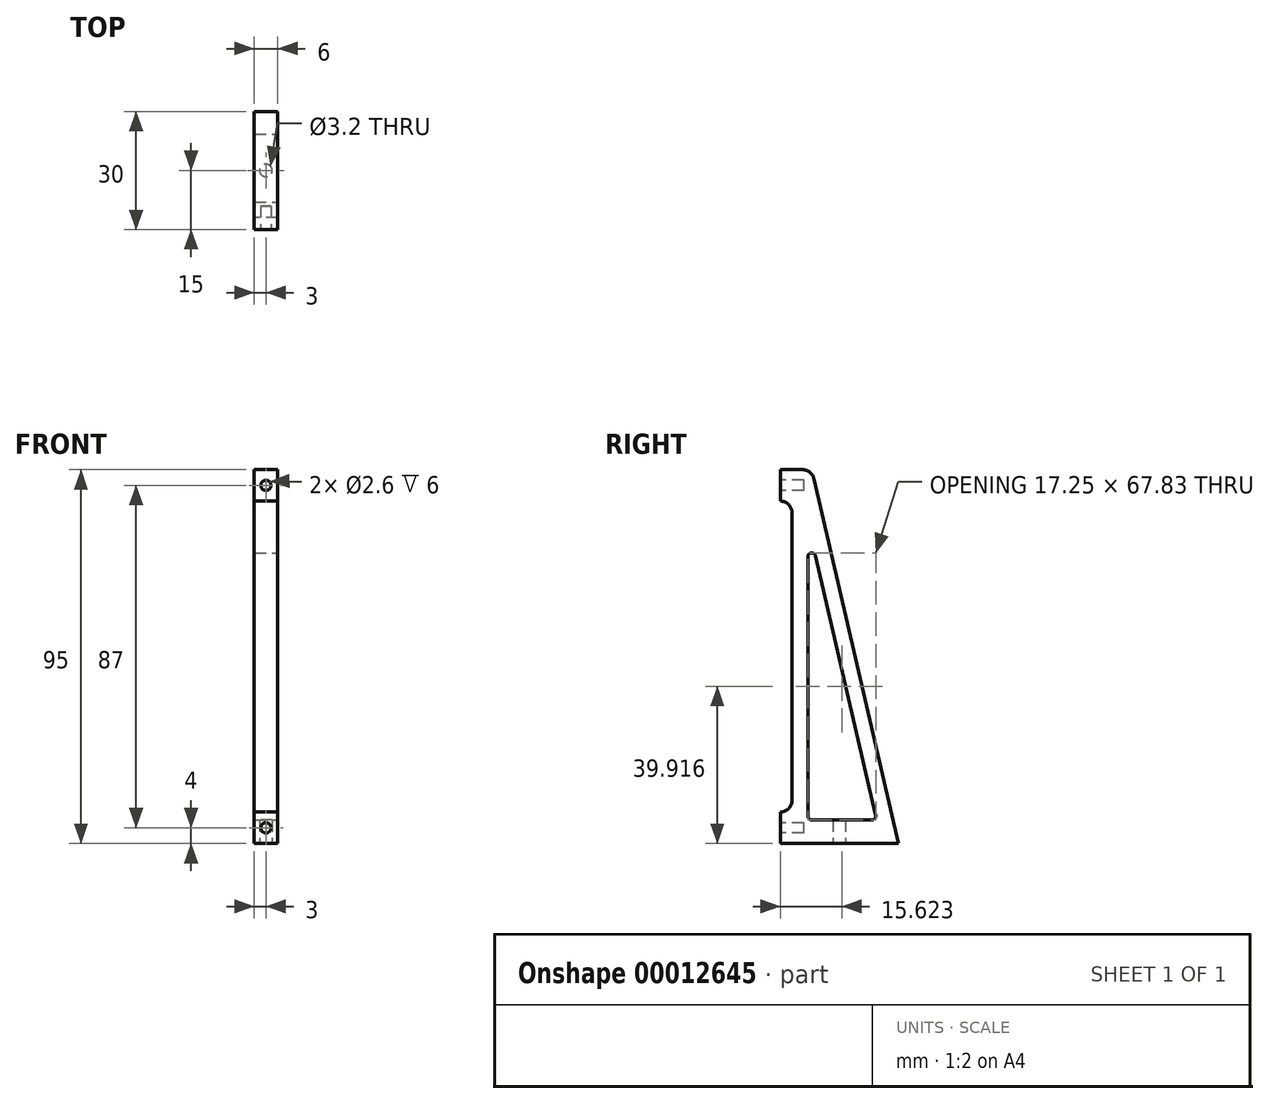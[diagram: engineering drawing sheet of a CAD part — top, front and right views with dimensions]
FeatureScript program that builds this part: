
annotation { "Feature Type Name" : "Feature", "Feature Type Description" : "" }
export const myFeature = defineFeature(function(context is Context, id is Id, definition is map)
    precondition{}
    {
        {
            var Q0;
            Q0=qCreatedBy(makeId("Right.planeOp"),FACE);
            var sketch = newSketch(context, id + "F0", { "sketchPlane" : qUnion([Q0])});
            skLineSegment(sketch, "E0", {"start": v(0, 0) * mm, "end": v(30, 0) * mm});
            skLineSegment(sketch, "E1", {"start": v(0, 0) * mm, "end": v(0, 8) * mm});
            skLineSegment(sketch, "E2", {"start": v(0, 8) * mm, "end": v(0, 8) * mm});
            skLineSegment(sketch, "E3", {"start": v(3, 11) * mm, "end": v(3, 84) * mm});
            skLineSegment(sketch, "E4", {"start": v(0, 87) * mm, "end": v(0, 87) * mm});
            skLineSegment(sketch, "E5", {"start": v(0, 87) * mm, "end": v(0, 95) * mm});
            skLineSegment(sketch, "E6", {"start": v(0, 95) * mm, "end": v(5.62, 95) * mm});
            skLineSegment(sketch, "E7", {"start": v(8.54, 92.68) * mm, "end": v(30, 0) * mm});
            skLineSegment(sketch, "E8", {"start": v(0, 91) * mm, "end": v(8.93, 91) * mm, "construction": true});
            skLineSegment(sketch, "E9", {"start": v(0, 4) * mm, "end": v(29.07, 4) * mm, "construction": true});
            skPoint(sketch, "E10.visualSharp", {"position": v(8, 95) * mm});
            skArc(sketch, "E10.filletArc", {"start": v(8.54, 92.68) * mm, "mid": v(7.48, 94.35) * mm, "end": v(5.62, 95) * mm});
            skPoint(sketch, "E11.visualSharp", {"position": v(3, 87) * mm});
            skArc(sketch, "E11.filletArc", {"start": v(3, 84) * mm, "mid": v(2.12, 86.12) * mm, "end": v(0, 87) * mm});
            skPoint(sketch, "E12.visualSharp", {"position": v(3, 8) * mm});
            skArc(sketch, "E12.filletArc", {"start": v(0, 8) * mm, "mid": v(2.12, 8.88) * mm, "end": v(3, 11) * mm});
            skSolve(sketch);
        }
        {
            var Q0;
            Q0 = qSketchRegion(id + "F0", true);
            extrude(context, id + "F1", {"entities" : qUnion([Q0]), "depth" : 3 * mm, "hasSecondDirection" : true, "secondDirectionOppositeDirection" : true, "secondDirectionDepth" : 3 * mm});
        }
        {
            var Q0;
            Q0=qCreatedBy(makeId("Right.planeOp"),FACE);
            var sketch = newSketch(context, id + "F2", { "sketchPlane" : qUnion([Q0])});
            skLineSegment(sketch, "E13", {"start": v(8.97, 73.06) * mm, "end": v(24.22, 7.23) * mm});
            skLineSegment(sketch, "E14", {"start": v(23.25, 6) * mm, "end": v(8, 6) * mm});
            skLineSegment(sketch, "E15", {"start": v(7, 7) * mm, "end": v(7, 72.84) * mm});
            skPoint(sketch, "E16.visualSharp", {"position": v(7, 81.59) * mm});
            skArc(sketch, "E16.filletArc", {"start": v(8.97, 73.06) * mm, "mid": v(7.89, 73.83) * mm, "end": v(7, 72.84) * mm});
            skPoint(sketch, "E17.visualSharp", {"position": v(7, 6) * mm});
            skArc(sketch, "E17.filletArc", {"start": v(7, 7) * mm, "mid": v(7.3, 6.3) * mm, "end": v(8, 6) * mm});
            skPoint(sketch, "E18.visualSharp", {"position": v(24.5, 6) * mm});
            skArc(sketch, "E18.filletArc", {"start": v(23.25, 6) * mm, "mid": v(24.03, 6.38) * mm, "end": v(24.22, 7.23) * mm});
            skSolve(sketch);
        }
        {
            var Q0;
            Q0 = qSketchRegion(id + "F2", true);
            extrude(context, id + "F3", {"entities" : qUnion([Q0]), "operationType" : NewBodyOperationType.REMOVE, "endBound" : BoundingType.UP_TO_NEXT, "oppositeDirection" : true, "depth" : 25 * mm, "hasSecondDirection" : true, "secondDirectionBound" : BoundingType.UP_TO_NEXT, "secondDirectionOppositeDirection" : false, "secondDirectionDepth" : 25 * mm});
        }
        {
            var Q0;
            Q0=makeQuery(id+"F1.opExtrude","SWEPT_FACE",FACE,{"disambiguationData":[OSD([sQuery(id+"F0.wireOp",EDGE,"E5")])]});
            var sketch = newSketch(context, id + "F4", { "sketchPlane" : qUnion([Q0])});
            skCircle(sketch, "E19", {"center": v(0, 91) * mm, "radius": 1.3 * mm});
            skCircle(sketch, "E20", {"center": v(0, 4) * mm, "radius": 1.3 * mm});
            skSolve(sketch);
        }
        {
            var Q0;
            Q0 = qSketchRegion(id + "F4", true);
            extrude(context, id + "F5", {"entities" : qUnion([Q0]), "operationType" : NewBodyOperationType.REMOVE, "oppositeDirection" : true, "depth" : 6 * mm});
        }
        {
            var Q0;
            Q0=makeQuery(id+"F1.opExtrude","SWEPT_FACE",FACE,{"disambiguationData":[OSD([sQuery(id+"F0.wireOp",EDGE,"E0")])]});
            var sketch = newSketch(context, id + "F6", { "sketchPlane" : qUnion([Q0])});
            skCircle(sketch, "E21", {"center": v(0, -15) * mm, "radius": 1.6 * mm});
            skSolve(sketch);
        }
        {
            var Q0;
            Q0 = qSketchRegion(id + "F6", true);
            extrude(context, id + "F7", {"entities" : qUnion([Q0]), "operationType" : NewBodyOperationType.REMOVE, "endBound" : BoundingType.UP_TO_NEXT, "oppositeDirection" : true, "depth" : 25 * mm});
        }
    });
